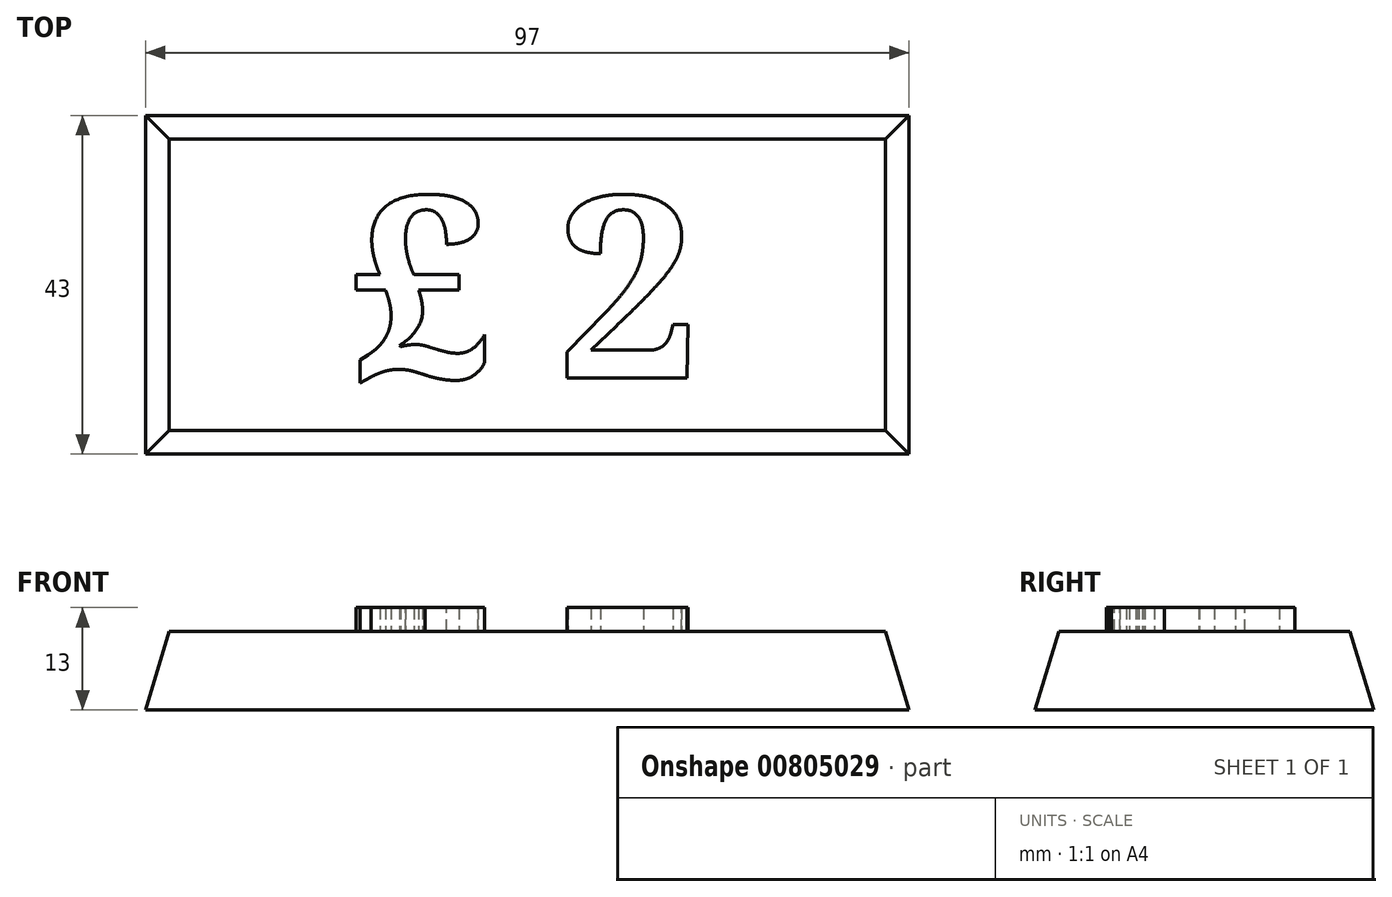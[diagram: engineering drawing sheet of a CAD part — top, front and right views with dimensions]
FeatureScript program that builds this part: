
annotation { "Feature Type Name" : "Feature", "Feature Type Description" : "" }
export const myFeature = defineFeature(function(context is Context, id is Id, definition is map)
    precondition{}
    {
        {
            var Q0;
            Q0=qCreatedBy(makeId("Top.planeOp"),FACE);
            var sketch = newSketch(context, id + "F0", { "sketchPlane" : qUnion([Q0])});
            skLineSegment(sketch, "E0.bottom", {"start": v(-53.25, -24.82) * mm, "end": v(43.75, -24.82) * mm});
            skLineSegment(sketch, "E0.top", {"start": v(-53.25, 18.18) * mm, "end": v(43.75, 18.18) * mm});
            skLineSegment(sketch, "E0.left", {"start": v(-53.25, -24.82) * mm, "end": v(-53.25, 18.18) * mm});
            skLineSegment(sketch, "E0.right", {"start": v(43.75, -24.82) * mm, "end": v(43.75, 18.18) * mm});
            skSolve(sketch);
        }
        {
            var Q0;
            Q0 = qSketchRegion(id + "F0", true);
            extrude(context, id + "F1", {"entities" : qUnion([Q0]), "depth" : 10 * mm, "offsetDistance" : 25.4 * mm, "hasDraft" : true, "draftAngle" : 16.7 * degree, "draftPullDirection" : true});
        }
        {
            var Q0;
            Q0=makeQuery(id+"F1.opExtrude","CAP_FACE",FACE,{"disambiguationData":[OSD([sQuery(id+"F0.wireOp",EDGE,"E0.bottom"),sQuery(id+"F0.wireOp",EDGE,"E0.top"),sQuery(id+"F0.wireOp",EDGE,"E0.left"),sQuery(id+"F0.wireOp",EDGE,"E0.right")])],"isStart":false});
            var sketch = newSketch(context, id + "F2", { "sketchPlane" : qUnion([Q0])});
            skText(sketch, "E1", { "text": "£ 2", "fontName": "NotoSerif-Bold.ttf"});
            const initialGuessF2  = {"E1": [-0.02725, -0.01515, 1, 0, 0.0232]};
            skSetInitialGuess(sketch, initialGuessF2);
            skSolve(sketch);
        }
        {
            var Q0;
            Q0 = qSketchRegion(id + "F2", true);
            extrude(context, id + "F3", {"entities" : qUnion([Q0]), "operationType" : NewBodyOperationType.ADD, "depth" : 3 * mm, "offsetDistance" : 25 * mm});
        }
    });
